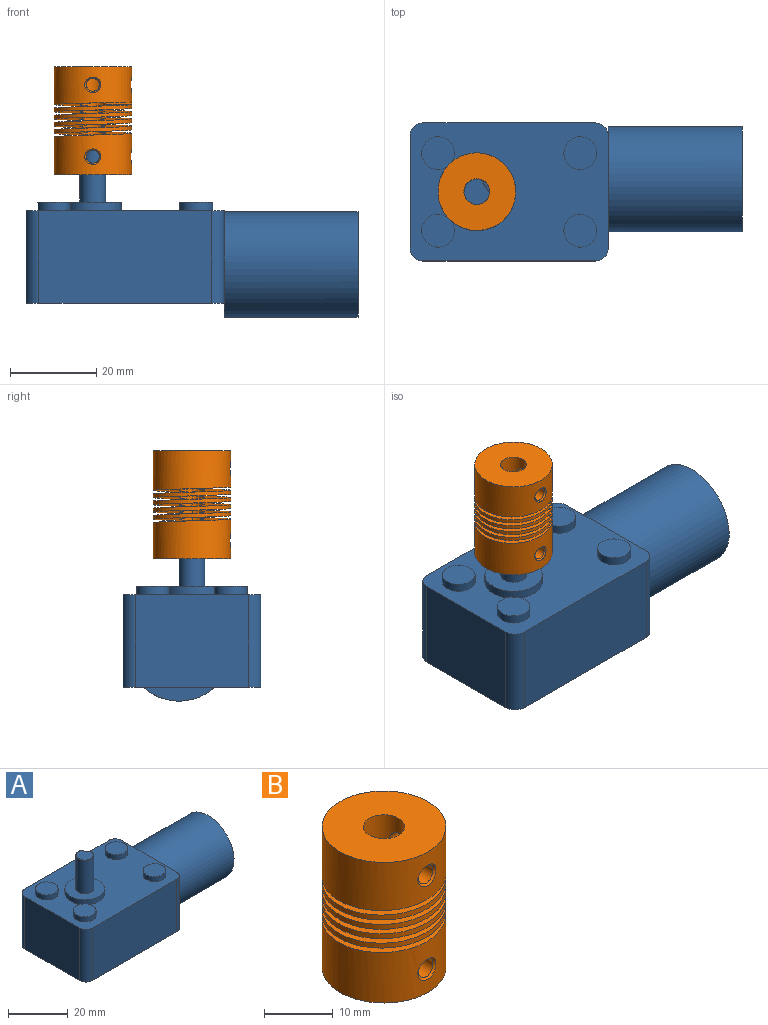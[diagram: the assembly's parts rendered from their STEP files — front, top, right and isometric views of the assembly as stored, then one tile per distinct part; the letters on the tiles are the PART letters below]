
ASSEMBLY  parts=2 mates=1
PART A: 31 faces, bbox 77x32x40.4 mm
  f0: plane 13.3x13.3mm, normal (0,0,1), area 110.7mm2, adj f20,f25
  f1: plane 2.01x1.76mm, normal (1,0,0), area 1.6mm2, adj f3,f11,f22
  f2: plane 26x21.5mm, normal (1,0,0), area 146.8mm2, adj f3,f9,f10,f11,f22
  f3: cylinder r=3mm len=21.5mm, axis (0,0,-1), area 101.3mm2, adj f1,f2,f4,f10,f11,f24
  f4: plane 40x21.5mm, normal (0,1,0), area 860mm2, adj f3,f5,f10,f11
  f5: cylinder r=3mm len=21.5mm, axis (0,0,-1), area 101.3mm2, adj f4,f6,f10,f11
  f6: plane 26x21.5mm, normal (-1,0,0), area 559mm2, adj f5,f7,f10,f11
  f7: cylinder r=3mm len=21.5mm, axis (0,0,-1), area 101.3mm2, adj f6,f8,f10,f11
  f8: plane 40x21.5mm, normal (0,-1,0), area 860mm2, adj f7,f9,f10,f11
  f9: cylinder r=3mm len=21.5mm, axis (0,0,-1), area 101.3mm2, adj f2,f8,f10,f11
  f10: plane 46x32mm, normal (0,0,1), area 1143.9mm2, adj f2,f3,f4,f5,f6,f7,f8,f9
  f11: plane 46x32mm, normal (0,0,-1), area 1464.3mm2, adj f1,f2,f3,f4,f5,f6,f7,f8
  f12: cylinder r=3.8mm len=7.6mm, axis (0,0,-1), area 47.8mm2, adj f10,f13
  f13: plane 7.6x7.6mm, normal (0,0,1), area 45.4mm2, adj f12
  f14: cylinder r=3.8mm len=7.6mm, axis (0,0,-1), area 47.8mm2, adj f10,f15
  f15: plane 7.6x7.6mm, normal (0,0,1), area 45.4mm2, adj f14
  f16: cylinder r=3.8mm len=7.6mm, axis (0,0,-1), area 47.8mm2, adj f10,f17
  f17: plane 7.6x7.6mm, normal (0,0,1), area 45.4mm2, adj f16
  f18: cylinder r=3.8mm len=7.6mm, axis (0,0,-1), area 47.8mm2, adj f10,f19
  f19: plane 7.6x7.6mm, normal (0,0,1), area 45.4mm2, adj f18
  f20: cylinder r=6.65mm len=13.3mm, axis (0,0,-1), area 83.6mm2, adj f0,f10
  f21: plane 16.47x3.2mm, normal (-1,0,0), area 36.2mm2, adj f11,f22
  f22: cylinder r=12.2mm len=31mm, axis (-1,0,0), area 2376.3mm2, adj f1,f2,f21,f23,f24
  f23: plane 24.4x24.4mm, normal (1,0,0), area 467.6mm2, adj f22
  f24: plane 13.98x2.2mm, normal (-1,0,0), area 20.9mm2, adj f3,f22
  f25: cylinder r=3mm len=13.6mm, axis (0,0,-1), area 214.3mm2, adj f0,f26,f27,f29
  f26: plane 2.96x2.05mm, normal (0,0,1), area 1.5mm2, adj f25,f27
  f27: plane 10.9x2.96mm, normal (0.82,0.57,0), area 39.2mm2, adj f25,f26,f30
  f28: plane 5.8x5.8mm, normal (0,0,1), area 25mm2, adj f29,f30
  f29: cone r=2.9mm half-angle=45deg, axis (0,0,-1), area 2.1mm2, adj f25,f28,f30
  f30: plane 2.99x2.11mm, normal (0.58,0.4,0.71), area 0.5mm2, adj f27,f28,f29
PART B: 28 faces, bbox 18x20.8x25 mm
  f0: cylinder r=1.5mm len=5.7mm, axis (0,-1,0), area 53.7mm2, adj f4,f25
  f1: cylinder r=1.5mm len=5.7mm, axis (0,-1,0), area 53.7mm2, adj f3,f26
  f2: plane 8.98x8.79mm, normal (0,0,-1), area 54mm2, adj f4,f10,f17,f19
  f3: cylinder r=3mm len=9.6mm, axis (0,0,-1), area 151.6mm2, adj f1,f8,f16,f18,f20,f21,f23
  f4: cylinder r=3mm len=9.6mm, axis (0,0,-1), area 151.6mm2, adj f0,f2,f5,f9,f17,f19,f22
  f5: cylinder r=3mm len=6mm, axis (0,0,-1), area 16.4mm2, adj f4,f6,f16,f19
  f6: cylinder r=3mm len=6mm, axis (0,0,-1), area 16.5mm2, adj f5,f7,f16,f19
  f7: cylinder r=3mm len=6mm, axis (0,0,-1), area 16.4mm2, adj f6,f8,f16,f19
  f8: cylinder r=3mm len=6mm, axis (0,0,-1), area 16.5mm2, adj f3,f7,f16,f19
  f9: plane 18x18mm, normal (0,0,1), area 226.2mm2, adj f4,f10
  f10: cylinder r=9mm len=18mm, axis (0,0,-1), area 477.4mm2, adj f2,f9,f12,f17,f19,f24,f25
  f11: cylinder r=9mm len=18mm, axis (0,0,-1), area 477.5mm2, adj f15,f16,f18,f20,f21,f26,f27
  f12: cylinder r=9mm len=18mm, axis (0,0,-1), area 49.3mm2, adj f10,f13,f16,f19
  f13: cylinder r=9mm len=18mm, axis (0,0,-1), area 49.4mm2, adj f12,f14,f16,f19
  f14: cylinder r=9mm len=18mm, axis (0,0,-1), area 49.3mm2, adj f13,f15,f16,f19
  f15: cylinder r=9mm len=18mm, axis (0,0,-1), area 49.4mm2, adj f11,f14,f16,f19
  f16: bspline ~20.78x18mm, area 1078.2mm2, adj f3,f5,f6,f7,f8,f11,f12,f13
  f17: plane 6x0.4mm, normal (0,-1,0), area 2.4mm2, adj f2,f4,f10,f16
  f18: plane 6x0.4mm, normal (0,1,0), area 2.4mm2, adj f3,f11,f19,f20
  f19: bspline ~18x17.97mm, area 1078.2mm2, adj f2,f4,f5,f6,f7,f8,f10,f12
  f20: plane 8.98x8.79mm, normal (0,0,1), area 54mm2, adj f3,f11,f16,f18
  f21: plane 18x18mm, normal (0,0,-1), area 226.2mm2, adj f3,f11
  f22: cylinder r=1.5mm len=5.7mm, axis (1,0,0), area 53.7mm2, adj f4,f24
  f23: cylinder r=1.5mm len=5.7mm, axis (1,0,0), area 53.7mm2, adj f3,f27
  f24: bspline ~3.72x3.6mm, area 4.7mm2, adj f10,f22
  f25: bspline ~3.72x3.6mm, area 4.7mm2, adj f0,f10
  f26: bspline ~3.72x3.6mm, area 4.7mm2, adj f1,f11
  f27: bspline ~3.72x3.6mm, area 4.7mm2, adj f11,f23
PLACE A t=(-14.64,6.64,-14.13)mm
PLACE B t=(-22.14,6.64,15.72)mm
MATE fastened B.f3 <-> A.f20  axis (0,0,1) through (-22.14,6.64,15.72)mm
